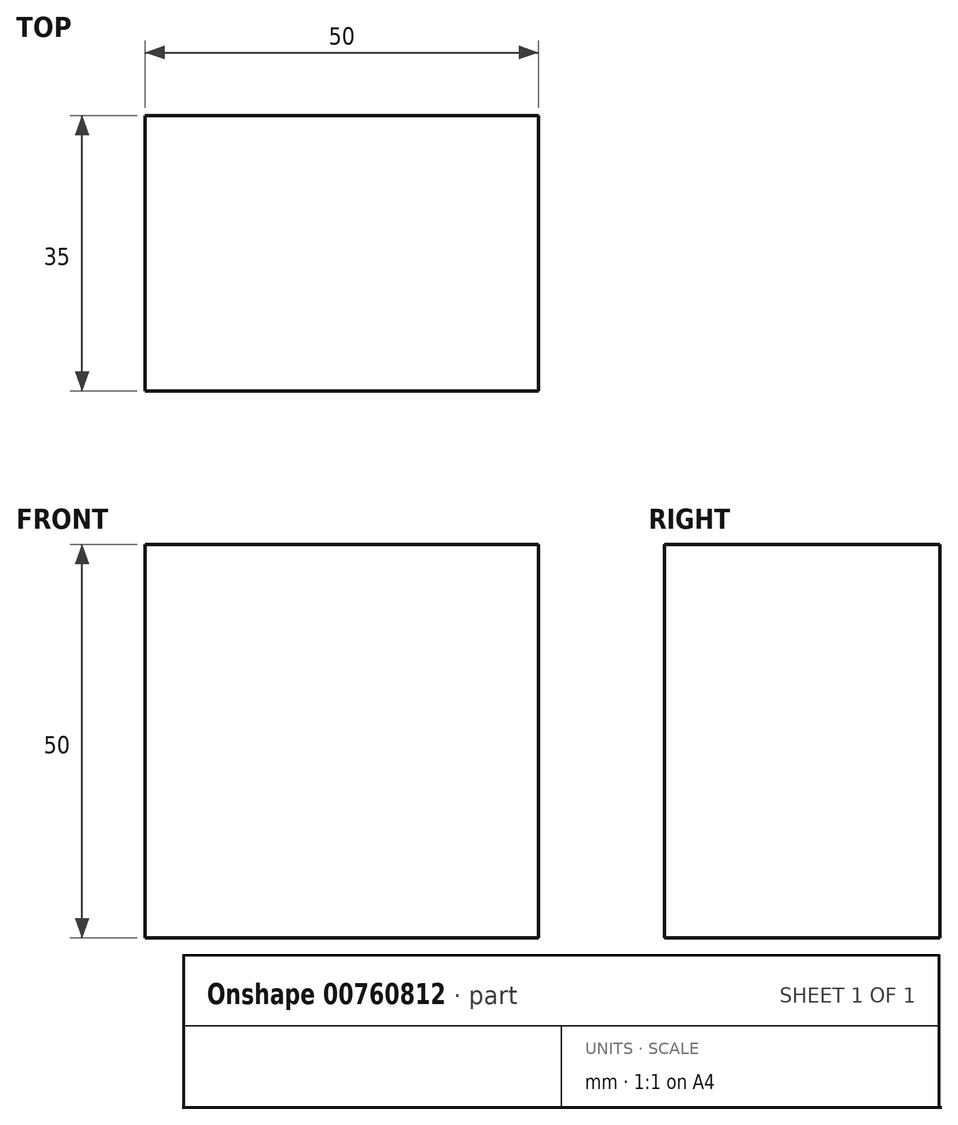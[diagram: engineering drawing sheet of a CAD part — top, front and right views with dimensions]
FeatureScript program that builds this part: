
annotation { "Feature Type Name" : "Feature", "Feature Type Description" : "" }
export const myFeature = defineFeature(function(context is Context, id is Id, definition is map)
    precondition{}
    {
        {
            var Q0;
            Q0=qCreatedBy(makeId("Front.planeOp"),FACE);
            var sketch = newSketch(context, id + "F0", { "sketchPlane" : qUnion([Q0])});
            skLineSegment(sketch, "E0.bottom", {"start": v(-26.16, 27.83) * mm, "end": v(23.84, 27.83) * mm});
            skLineSegment(sketch, "E0.top", {"start": v(-26.16, -22.17) * mm, "end": v(23.84, -22.17) * mm});
            skLineSegment(sketch, "E0.left", {"start": v(-26.16, 27.83) * mm, "end": v(-26.16, -22.17) * mm});
            skLineSegment(sketch, "E0.right", {"start": v(23.84, 27.83) * mm, "end": v(23.84, -22.17) * mm});
            skSolve(sketch);
        }
        {
            var Q0;
            Q0=makeQuery(id+"F0.imprint","IMPRINT",FACE,{"disambiguationData":[TD([[makeQuery(id+"F0.imprint","IMPRINT",EDGE,{"derivedFrom":sQuery(id+"F0.wireOp",EDGE,"E0.bottom")}),-1.0]])]});
            extrude(context, id + "F1", {"entities" : qUnion([Q0]), "depth" : 10 * mm, "offsetDistance" : 25 * mm});
        }
        {
            var Q0;
            Q0=makeQuery(id+"F1.opExtrude","CAP_FACE",FACE,{"disambiguationData":[OSD([sQuery(id+"F0.wireOp",EDGE,"E0.bottom"),sQuery(id+"F0.wireOp",EDGE,"E0.top"),sQuery(id+"F0.wireOp",EDGE,"E0.left"),sQuery(id+"F0.wireOp",EDGE,"E0.right")])],"isStart":true});
            var sketch = newSketch(context, id + "F2", { "sketchPlane" : qUnion([Q0])});
            skLineSegment(sketch, "E1.bottom", {"start": v(-15.6, 18.9) * mm, "end": v(-7.03, 18.9) * mm});
            skLineSegment(sketch, "E1.top", {"start": v(-15.6, -11) * mm, "end": v(-7.03, -11) * mm});
            skLineSegment(sketch, "E1.left", {"start": v(-15.6, 18.9) * mm, "end": v(-15.6, -11) * mm});
            skLineSegment(sketch, "E1.right", {"start": v(-7.03, 18.9) * mm, "end": v(-7.03, -11) * mm});
            skSolve(sketch);
        }
        {
            var Q0;
            Q0=makeQuery(id+"F2.imprint","IMPRINT",FACE,{"disambiguationData":[TD([[makeQuery(id+"F2.imprint","IMPRINT",EDGE,{"derivedFrom":sQuery(id+"F2.wireOp",EDGE,"E1.bottom")}),-1.0]])]});
            var sketch = newSketch(context, id + "F3", { "sketchPlane" : qUnion([Q0])});
            skSolve(sketch);
        }
        {
            var Q0;
            Q0=makeQuery(id+"F2.imprint","IMPRINT",FACE,{"disambiguationData":[TD([[makeQuery(id+"F2.imprint","IMPRINT",EDGE,{"derivedFrom":sQuery(id+"F2.wireOp",EDGE,"E1.bottom")}),1.0]])]});
            var sketch = newSketch(context, id + "F4", { "sketchPlane" : qUnion([Q0])});
            skLineSegment(sketch, "E2.bottom", {"start": v(6.42, 18.6) * mm, "end": v(15, 18.6) * mm});
            skLineSegment(sketch, "E2.top", {"start": v(6.42, -11.3) * mm, "end": v(15, -11.3) * mm});
            skLineSegment(sketch, "E2.left", {"start": v(6.42, 18.6) * mm, "end": v(6.42, -11.3) * mm});
            skLineSegment(sketch, "E2.right", {"start": v(15, 18.6) * mm, "end": v(15, -11.3) * mm});
            skSolve(sketch);
        }
        {
            var Q0;
            Q0=makeQuery(id+"F4.imprint","IMPRINT",FACE,{"disambiguationData":[TD([[makeQuery(id+"F4.imprint","IMPRINT",EDGE,{"derivedFrom":sQuery(id+"F4.wireOp",EDGE,"E2.bottom")}),-1.0]])]});
            var Q1;
            Q1=makeQuery(id+"F3.imprint","IMPRINT",FACE,{"disambiguationData":[TD([[makeQuery(id+"F3.imprint","IMPRINT",EDGE,{"derivedFrom":makeQuery(id+"F2.imprint","IMPRINT",EDGE,{"derivedFrom":sQuery(id+"F2.wireOp",EDGE,"E1.bottom")})}),-1.0]])]});
            var Q2;
            Q2=makeQuery(id+"F2.imprint","IMPRINT",FACE,{"disambiguationData":[TD([[makeQuery(id+"F2.imprint","IMPRINT",EDGE,{"derivedFrom":sQuery(id+"F2.wireOp",EDGE,"E1.bottom")}),-1.0]])]});
            var Q3;
            Q3=makeQuery(id+"F4.imprint","IMPRINT",FACE,{"disambiguationData":[TD([[makeQuery(id+"F4.imprint","IMPRINT",EDGE,{"derivedFrom":sQuery(id+"F4.wireOp",EDGE,"E2.bottom")}),1.0]])]});
            var Q4;
            Q4=makeQuery(id+"F4.imprint","IMPRINT",FACE,{"disambiguationData":[TD([[makeQuery(id+"F4.imprint","IMPRINT",EDGE,{"derivedFrom":makeQuery(id+"F2.imprint","IMPRINT",EDGE,{"derivedFrom":sQuery(id+"F2.wireOp",EDGE,"E1.bottom")})}),-1.0]])]});
            var Q5;
            Q5=makeQuery(id+"F1.opExtrude","CAP_FACE",FACE,{"disambiguationData":[OSD([sQuery(id+"F0.wireOp",EDGE,"E0.bottom"),sQuery(id+"F0.wireOp",EDGE,"E0.top"),sQuery(id+"F0.wireOp",EDGE,"E0.left"),sQuery(id+"F0.wireOp",EDGE,"E0.right")])],"isStart":true});
            var Q6;
            Q6=makeQuery(id+"F1.opExtrude","CAP_FACE",FACE,{"disambiguationData":[OSD([sQuery(id+"F0.wireOp",EDGE,"E0.bottom"),sQuery(id+"F0.wireOp",EDGE,"E0.top"),sQuery(id+"F0.wireOp",EDGE,"E0.left"),sQuery(id+"F0.wireOp",EDGE,"E0.right")])],"isStart":false});
            extrude(context, id + "F5", {"entities" : qUnion([Q0, Q1, Q2, Q3, Q4, Q5, Q6]), "operationType" : NewBodyOperationType.ADD, "depth" : 25 * mm, "offsetDistance" : 25 * mm});
        }
    });
